# Revit family: Neptun Domus
name_source: partatom
category: HLS-Bauteile
units: mm (PartAtom-declared; Revit-internal decimal feet)

## family parameters
Arbeitsebenenbasiert = Nein
Beim Laden mit Abzugskörper schneiden = Nein
Bemaßung runder Anschluss = Durchmesser verwenden
Beschriftungsausrichtung beibehalten = Nein
Gemeinsam genutzt = Nein
Immer vertikal = Ja
Klassifizierung = Keine
Raumberechnungspunkt = Nein
Teiletyp = Normal

## types (3) — shared parameters
Anschluss 5/4" = 20 mm  [stored 0.0656168 ft]
Behälterkopf = 100 mm  [stored 0.328084 ft]
Datenblatt = https://www.burkhalter-h2o.ch
Homepage = https://www.burkhalter-h2o.ch
LUT = LUT_Neptun_Domus
Sockel_Höhe = 100 mm  [stored 0.328084 ft]
Steuerung_Breite = 175 mm  [stored 0.574147 ft]
Steuerung_Höhe = 175 mm  [stored 0.574147 ft]
Steuerung_Tiefe = 75 mm  [stored 0.246063 ft]
zero-valued in all types: Vorgabe-Ansicht

## per-type parameters (varying)
| type | A | B | C | Harzinhalt_pro_Harzdruckbehälter | Sockel_Absatz_Oben | Sockel_Absatz_Unten |
| Neptun Domus - 15L | 208 mm | 1100 mm  [stored 3.60892 ft] | 960 mm  [stored 3.14961 ft] | 15L | 114 mm  [stored 0.374016 ft] | 114 mm  [stored 0.374016 ft] |
| Neptun Domus - 25L | 257 mm  [stored 0.843176 ft] | 1100 mm  [stored 3.60892 ft] | 960 mm  [stored 3.14961 ft] | 25L | 139 mm | 139 mm |
| Neptun Domus - 50L | 304 mm  [stored 0.997375 ft] | 1430 mm  [stored 4.6916 ft] | 1290 mm  [stored 4.23228 ft] | 50L | 162 mm  [stored 0.531496 ft] | 162 mm  [stored 0.531496 ft] |

note: [stored X ft] marks values corroborated as IEEE doubles in the binary element streams (Revit-internal decimal feet)
